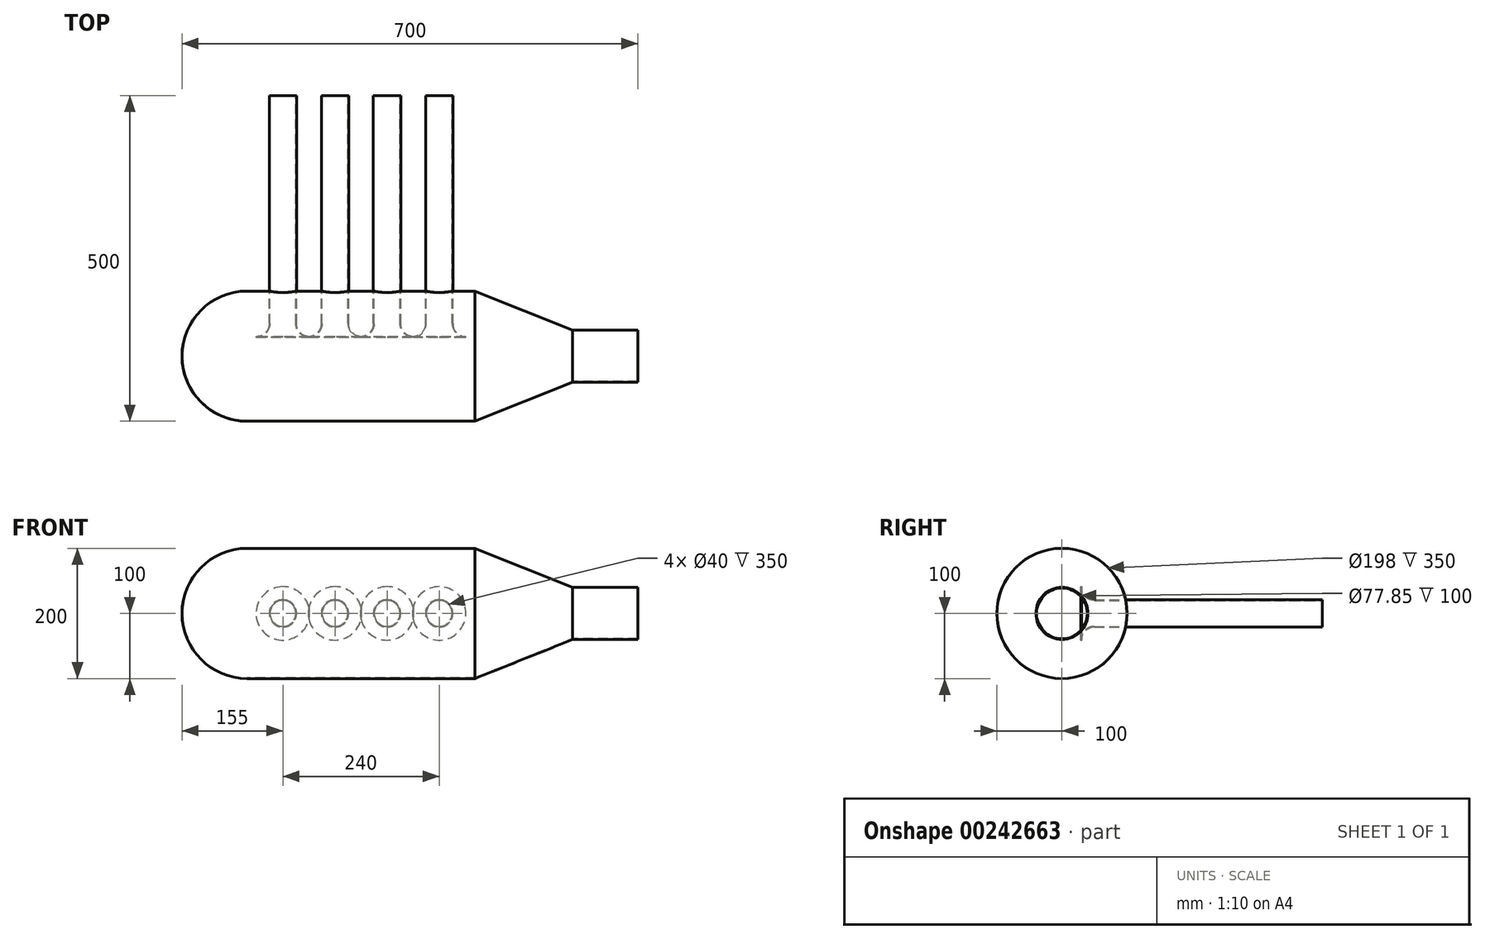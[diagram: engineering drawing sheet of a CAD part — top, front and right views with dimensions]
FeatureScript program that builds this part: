
annotation { "Feature Type Name" : "Feature", "Feature Type Description" : "" }
export const myFeature = defineFeature(function(context is Context, id is Id, definition is map)
    precondition{}
    {
        {
            var Q0;
            Q0=qCreatedBy(makeId("Front.planeOp"),FACE);
            var sketch = newSketch(context, id + "F0", { "sketchPlane" : qUnion([Q0])});
            skCircle(sketch, "E0", {"center": v(-120, 0) * mm, "radius": 21 * mm});
            skCircle(sketch, "E1", {"center": v(-40, 0) * mm, "radius": 21 * mm});
            skCircle(sketch, "E2", {"center": v(40, 0) * mm, "radius": 21 * mm});
            skCircle(sketch, "E3", {"center": v(120, 0) * mm, "radius": 21 * mm});
            skSolve(sketch);
        }
        {
            var Q0;
            Q0 = qSketchRegion(id + "F0", true);
            extrude(context, id + "F1", {"entities" : qUnion([Q0]), "depth" : 350 * mm});
        }
        {
            var Q0;
            Q0=qCreatedBy(makeId("Right.planeOp"),FACE);
            var sketch = newSketch(context, id + "F2", { "sketchPlane" : qUnion([Q0])});
            skCircle(sketch, "E4", {"center": v(-400, 0) * mm, "radius": 100 * mm});
            skCircle(sketch, "E5", {"center": v(-400, 0) * mm, "radius": 99 * mm});
            skSolve(sketch);
        }
        {
            var Q0;
            Q0 = qSketchRegion(id + "F2", true);
            extrude(context, id + "F3", {"entities" : qUnion([Q0]), "operationType" : NewBodyOperationType.ADD, "endBound" : BoundingType.SYMMETRIC, "depth" : 350 * mm});
        }
        {
            var Q0;
            Q0=makeQuery(id+"F1.opExtrude","CAP_FACE",FACE,{"disambiguationData":[OSD([sQuery(id+"F0.wireOp",EDGE,"E3")])],"isStart":true});
            var Q1;
            Q1=makeQuery(id+"F1.opExtrude","CAP_FACE",FACE,{"disambiguationData":[OSD([sQuery(id+"F0.wireOp",EDGE,"E2")])],"isStart":true});
            var Q2;
            Q2=makeQuery(id+"F1.opExtrude","CAP_FACE",FACE,{"disambiguationData":[OSD([sQuery(id+"F0.wireOp",EDGE,"E1")])],"isStart":true});
            var Q3;
            Q3=makeQuery(id+"F1.opExtrude","CAP_FACE",FACE,{"disambiguationData":[OSD([sQuery(id+"F0.wireOp",EDGE,"E0")])],"isStart":true});
            var Q4;
            Q4=makeQuery(id+"F1.opExtrude","CAP_FACE",FACE,{"disambiguationData":[OSD([sQuery(id+"F0.wireOp",EDGE,"E0")])],"isStart":false});
            var Q5;
            Q5=makeQuery(id+"F1.opExtrude","CAP_FACE",FACE,{"disambiguationData":[OSD([sQuery(id+"F0.wireOp",EDGE,"E1")])],"isStart":false});
            var Q6;
            Q6=makeQuery(id+"F1.opExtrude","CAP_FACE",FACE,{"disambiguationData":[OSD([sQuery(id+"F0.wireOp",EDGE,"E2")])],"isStart":false});
            var Q7;
            Q7=makeQuery(id+"F1.opExtrude","CAP_FACE",FACE,{"disambiguationData":[OSD([sQuery(id+"F0.wireOp",EDGE,"E3")])],"isStart":false});
            shell(context, id + "F4", {"entities" : qUnion([Q0, Q1, Q2, Q3, Q4, Q5, Q6, Q7]), "thickness" : 1 * mm});
        }
        {
            var Q0;
            Q0=qCreatedBy(makeId("Right.planeOp"),FACE);
            cPlane(context, id + "F5", {"entities" : qUnion([Q0]), "cplaneType" : CPlaneType.OFFSET, "offset" : (40 + 80) * mm, "width" : 150 * mm, "height" : 150 * mm});
        }
        {
            var Q0;
            Q0=qCreatedBy(id+"F5.planeOp",FACE);
            var sketch = newSketch(context, id + "F6", { "sketchPlane" : qUnion([Q0])});
            skLineSegment(sketch, "E6.0", {"start": v(-350, -21) * mm, "end": v(-350, 21) * mm, "construction": true});
            skArc(sketch, "E7", {"start": v(-370, 41) * mm, "mid": v(-364.14, 26.86) * mm, "end": v(-350, 21) * mm});
            skLineSegment(sketch, "E8", {"start": v(-350, 21) * mm, "end": v(-303.25, 21) * mm, "construction": true});
            skLineSegment(sketch, "E9", {"start": v(-303.25, -21) * mm, "end": v(-350, -21) * mm, "construction": true});
            skLineSegment(sketch, "E10", {"start": v(-350, 21) * mm, "end": v(-350, 58.31) * mm, "construction": true});
            skLineSegment(sketch, "E11", {"start": v(-350, 41) * mm, "end": v(-370, 41) * mm, "construction": true});
            skArc(sketch, "E12", {"start": v(-350, 20) * mm, "mid": v(-364.85, 26.15) * mm, "end": v(-371, 41) * mm});
            skLineSegment(sketch, "E13", {"start": v(-350, 20) * mm, "end": v(-350, 21) * mm});
            skLineSegment(sketch, "E14", {"start": v(-370, 41) * mm, "end": v(-371, 41) * mm});
            skSolve(sketch);
        }
        {
            var Q0;
            Q0 = qSketchRegion(id + "F6", true);
            var Q1;
            {var subQ0=sQuery(id+"F0.wireOp",EDGE,"E3");Q1=makeQuery(id+"F4.opShell","OFFSET_EDGE",EDGE,{"disambiguationData":[OSD([subQ0]),TDD([makeQuery(id+"F1.opExtrude","CAP_EDGE",EDGE,{"disambiguationData":[OSD([subQ0])],"isStart":false})])]});}
            revolve(context, id + "F7", {"entities" : qUnion([Q0]), "axis" : qUnion([Q1]), "revolveType" : RevolveType.FULL});
        }
        {
            var Q0;
            Q0=makeQuery(id+"F7.opRevolve","SWEPT_BODY",BODY,{"disambiguationData":[OSD([sQuery(id+"F6.wireOp",EDGE,"E7"),sQuery(id+"F6.wireOp",EDGE,"E12"),sQuery(id+"F6.wireOp",EDGE,"E13"),sQuery(id+"F6.wireOp",EDGE,"E14")])]});
            var Q1;
            Q1=makeQuery(id+"F3.opExtrude","SWEPT_FACE",FACE,{"disambiguationData":[OSD([sQuery(id+"F2.wireOp",EDGE,"E4")])]});
            transform(context, id + "F8", {"entities" : qUnion([Q0]), "transformType" : TransformType.TRANSLATION_DISTANCE, "transformDirection" : qUnion([Q1]), "distance" : 80 * mm, "makeCopy" : true});
        }
        {
            var Q0;
            Q0=makeQuery(id+"F8.opPattern","COPY",BODY,{"derivedFrom":makeQuery(id+"F7.opRevolve","SWEPT_BODY",BODY,{"disambiguationData":[OSD([sQuery(id+"F6.wireOp",EDGE,"E7"),sQuery(id+"F6.wireOp",EDGE,"E12"),sQuery(id+"F6.wireOp",EDGE,"E13"),sQuery(id+"F6.wireOp",EDGE,"E14")])]}),"instanceName":"1"});
            var Q1;
            Q1=makeQuery(id+"F7.opRevolve","SWEPT_BODY",BODY,{"disambiguationData":[OSD([sQuery(id+"F6.wireOp",EDGE,"E7"),sQuery(id+"F6.wireOp",EDGE,"E12"),sQuery(id+"F6.wireOp",EDGE,"E13"),sQuery(id+"F6.wireOp",EDGE,"E14")])]});
            var Q2;
            Q2=qCreatedBy(makeId("Right.planeOp"),FACE);
            mirror(context, id + "F9", {"operationType" : NewBodyOperationType.ADD, "entities" : qUnion([Q0, Q1]), "mirrorPlane" : qUnion([Q2])});
        }
        {
            var Q0;
            Q0=qCreatedBy(makeId("Top.planeOp"),FACE);
            var sketch = newSketch(context, id + "F10", { "sketchPlane" : qUnion([Q0])});
            skLineSegment(sketch, "E15.0", {"start": v(-175, -300) * mm, "end": v(-175, -500) * mm, "construction": true});
            skLineSegment(sketch, "E16", {"start": v(175, -500) * mm, "end": v(-175, -500) * mm, "construction": true});
            skLineSegment(sketch, "E17", {"start": v(-175, -300) * mm, "end": v(175, -300) * mm, "construction": true});
            skLineSegment(sketch, "E18", {"start": v(-66.21, -400) * mm, "end": v(-411.88, -400) * mm, "construction": true});
            skArc(sketch, "E19", {"start": v(-175, -500) * mm, "mid": v(-245.71, -470.71) * mm, "end": v(-275, -400) * mm});
            skArc(sketch, "E20", {"start": v(-175, -499) * mm, "mid": v(-245, -470) * mm, "end": v(-274, -400) * mm});
            skLineSegment(sketch, "E21", {"start": v(-175, -499) * mm, "end": v(-175, -500) * mm});
            skLineSegment(sketch, "E22", {"start": v(-274, -400) * mm, "end": v(-275, -400) * mm});
            skSolve(sketch);
        }
        {
            var Q0;
            Q0 = qSketchRegion(id + "F10", true);
            var Q1;
            Q1=makeQuery(id+"F3.opExtrude","CAP_EDGE",EDGE,{"disambiguationData":[OSD([sQuery(id+"F2.wireOp",EDGE,"E4")])],"isStart":true});
            revolve(context, id + "F11", {"operationType" : NewBodyOperationType.ADD, "entities" : qUnion([Q0]), "axis" : qUnion([Q1]), "revolveType" : RevolveType.FULL});
        }
        {
            var Q0;
            Q0=makeQuery(id+"F3.opExtrude","CAP_FACE",FACE,{"disambiguationData":[OSD([sQuery(id+"F2.wireOp",EDGE,"E4"),sQuery(id+"F2.wireOp",EDGE,"E5")])],"isStart":false});
            var sketch = newSketch(context, id + "F12", { "sketchPlane" : qUnion([Q0])});
            skCircle(sketch, "E23.0", {"center": v(-400, 0) * mm, "radius": 100 * mm});
            skSolve(sketch);
        }
        {
            var Q0;
            Q0=makeQuery(id+"F12.imprint","IMPRINT",FACE,{"disambiguationData":[TD([[makeQuery(id+"F12.imprint","IMPRINT",EDGE,{"derivedFrom":sQuery(id+"F12.wireOp",EDGE,"E23.0")}),1.0]])]});
            cPlane(context, id + "F13", {"entities" : qUnion([Q0]), "cplaneType" : CPlaneType.OFFSET, "offset" : 150 * mm, "width" : 150 * mm, "height" : 150 * mm});
        }
        {
            var Q0;
            Q0=qCreatedBy(id+"F13.planeOp",FACE);
            var sketch = newSketch(context, id + "F14", { "sketchPlane" : qUnion([Q0])});
            skCircle(sketch, "E24", {"center": v(-400, 0) * mm, "radius": 40 * mm});
            skSolve(sketch);
        }
        {
            var Q1;
            Q1 = qSketchRegion(id + "F14", true);
            var Q2;
            Q2 = qSketchRegion(id + "F12", true);
            loft(context, id + "F15", {"sheetProfilesArray" : [{ "sheetProfileEntities" : qUnion([Q1]) }, { "sheetProfileEntities" : qUnion([Q2]) }]});
        }
        {
            var Q0;
            Q0=makeQuery(id+"F15.opLoft","CAP_FACE",FACE,{"disambiguationData":[OSD([makeQuery(id+"F12.imprint","IMPRINT",FACE,{"disambiguationData":[TD([[makeQuery(id+"F12.imprint","IMPRINT",EDGE,{"derivedFrom":makeQuery(id+"F3.opExtrude","CAP_EDGE",EDGE,{"disambiguationData":[OSD([sQuery(id+"F2.wireOp",EDGE,"E5")])],"isStart":false})}),1.0]])]})])],"isStart":true});
            var Q1;
            Q1=makeQuery(id+"F15.opLoft","CAP_FACE",FACE,{"disambiguationData":[OSD([makeQuery(id+"F14.imprint","IMPRINT",FACE,{"disambiguationData":[TD([[makeQuery(id+"F14.imprint","IMPRINT",EDGE,{"derivedFrom":sQuery(id+"F14.wireOp",EDGE,"E24")}),1.0]])]})])],"isStart":true});
            shell(context, id + "F16", {"entities" : qUnion([Q0, Q1]), "thickness" : 1 * mm});
        }
        {
            var Q0;
            Q0=makeQuery(id+"F15.opLoft","CAP_FACE",FACE,{"disambiguationData":[OSD([makeQuery(id+"F14.imprint","IMPRINT",FACE,{"disambiguationData":[TD([[makeQuery(id+"F14.imprint","IMPRINT",EDGE,{"derivedFrom":sQuery(id+"F14.wireOp",EDGE,"E24")}),1.0]])]})])],"isStart":true});
            var sketch = newSketch(context, id + "F17", { "sketchPlane" : qUnion([Q0])});
            skCircle(sketch, "E25.0", {"center": v(-400, 0) * mm, "radius": 38.92 * mm});
            skCircle(sketch, "E26.0", {"center": v(-400, 0) * mm, "radius": 40 * mm});
            skSolve(sketch);
        }
        {
            var Q0;
            Q0 = qSketchRegion(id + "F17", true);
            extrude(context, id + "F18", {"entities" : qUnion([Q0]), "operationType" : NewBodyOperationType.ADD, "depth" : 100 * mm});
        }
    });
